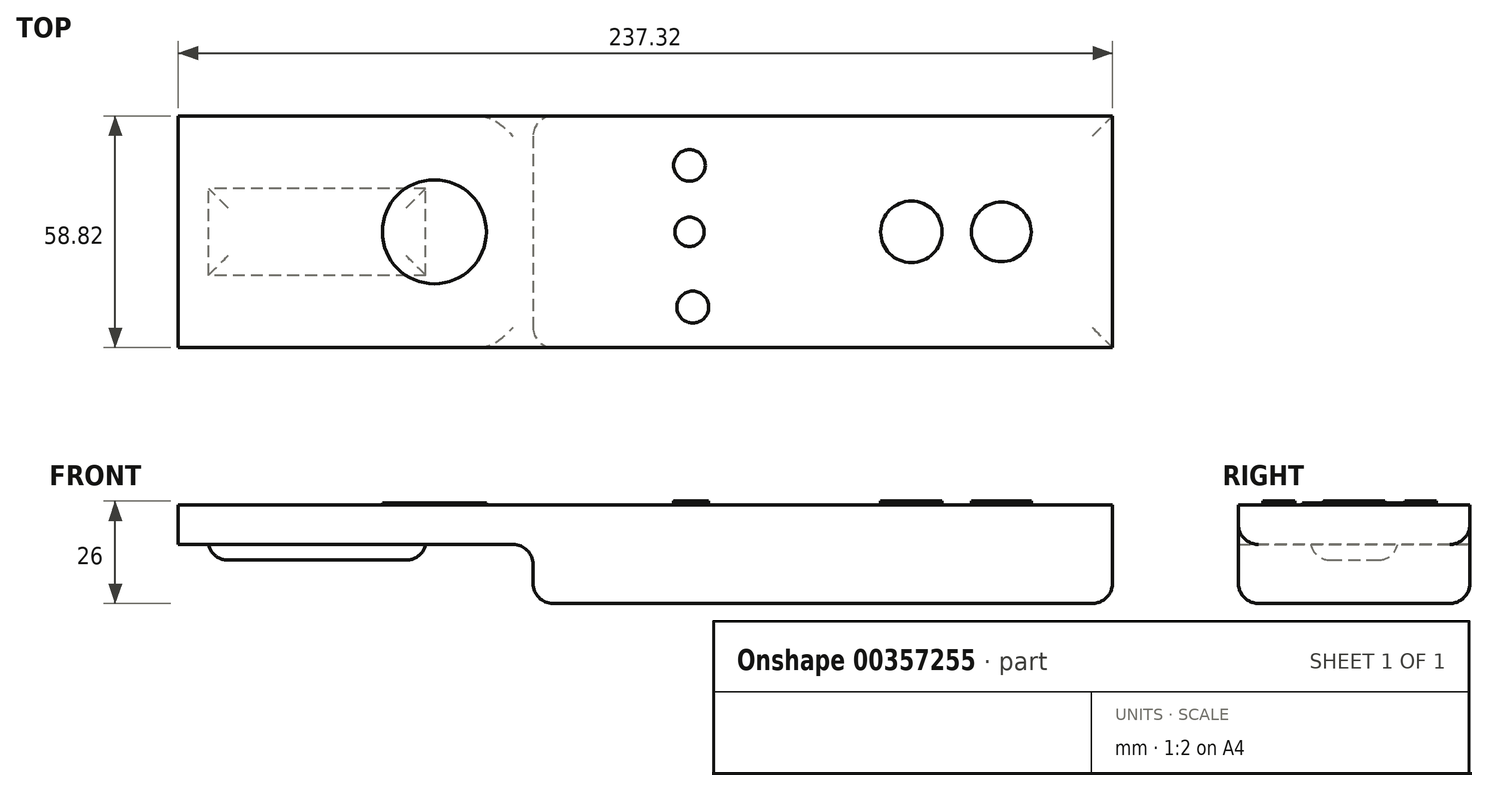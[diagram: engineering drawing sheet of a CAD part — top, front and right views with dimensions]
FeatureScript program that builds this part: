
annotation { "Feature Type Name" : "Feature", "Feature Type Description" : "" }
export const myFeature = defineFeature(function(context is Context, id is Id, definition is map)
    precondition{}
    {
        {
            var Q0;
            Q0=qCreatedBy(makeId("Top.planeOp"),FACE);
            var sketch = newSketch(context, id + "F0", { "sketchPlane" : qUnion([Q0])});
            skLineSegment(sketch, "E0.bottom", {"start": v(118.66, -29.4) * mm, "end": v(-118.66, -29.4) * mm});
            skLineSegment(sketch, "E0.top", {"start": v(118.66, 29.4) * mm, "end": v(-118.66, 29.4) * mm});
            skLineSegment(sketch, "E0.left", {"start": v(118.66, -29.4) * mm, "end": v(118.66, 29.4) * mm});
            skLineSegment(sketch, "E0.right", {"start": v(-118.66, -29.4) * mm, "end": v(-118.66, 29.4) * mm});
            skPoint(sketch, "E0.middle", {"position": v(0, 0) * mm});
            skSolve(sketch);
        }
        {
            var Q0;
            Q0 = qSketchRegion(id + "F0", true);
            extrude(context, id + "F1", {"entities" : qUnion([Q0]), "depth" : 10 * mm});
        }
        {
            var Q0;
            Q0=makeQuery(id+"F1.opExtrude","CAP_FACE",FACE,{"disambiguationData":[OSD([sQuery(id+"F0.wireOp",EDGE,"E0.bottom"),sQuery(id+"F0.wireOp",EDGE,"E0.top"),sQuery(id+"F0.wireOp",EDGE,"E0.left"),sQuery(id+"F0.wireOp",EDGE,"E0.right")])],"isStart":true});
            var sketch = newSketch(context, id + "F2", { "sketchPlane" : qUnion([Q0])});
            skLineSegment(sketch, "E1.bottom", {"start": v(118.66, -29.4) * mm, "end": v(-28.54, -29.4) * mm});
            skLineSegment(sketch, "E1.top", {"start": v(118.66, 29.4) * mm, "end": v(-28.54, 29.4) * mm});
            skLineSegment(sketch, "E1.left", {"start": v(118.66, -29.4) * mm, "end": v(118.66, 29.4) * mm});
            skLineSegment(sketch, "E1.right", {"start": v(-28.54, -29.4) * mm, "end": v(-28.54, 29.4) * mm});
            skPoint(sketch, "E1.middle", {"position": v(45.06, 0) * mm});
            skSolve(sketch);
        }
        {
            var Q0;
            Q0=makeQuery(id+"F2.imprint","IMPRINT",FACE,{"disambiguationData":[TD([[makeQuery(id+"F2.imprint","IMPRINT",EDGE,{"derivedFrom":sQuery(id+"F2.wireOp",EDGE,"E1.bottom")}),-1.0]])]});
            extrude(context, id + "F3", {"entities" : qUnion([Q0]), "operationType" : NewBodyOperationType.ADD, "depth" : 15 * mm});
        }
        {
            var Q0;
            Q0=makeQuery(id+"F3.opExtrude","SWEPT_FACE",FACE,{"disambiguationData":[OSD([sQuery(id+"F2.wireOp",EDGE,"E1.right")])]});
            var Q1;
            Q1=makeQuery(id+"F3.opExtrude","CAP_FACE",FACE,{"disambiguationData":[OSD([sQuery(id+"F2.wireOp",EDGE,"E1.bottom"),sQuery(id+"F2.wireOp",EDGE,"E1.top"),sQuery(id+"F2.wireOp",EDGE,"E1.left"),sQuery(id+"F2.wireOp",EDGE,"E1.right")])],"isStart":false});
            fillet(context, id + "F4", {"entities" : qUnion([Q0, Q1]), "radius" : 5.08 * mm, "tangentPropagation" : true, "allowEdgeOverflow" : false});
        }
        {
            var Q0;
            Q0=makeQuery(id+"F1.opExtrude","CAP_FACE",FACE,{"disambiguationData":[OSD([sQuery(id+"F0.wireOp",EDGE,"E0.bottom"),sQuery(id+"F0.wireOp",EDGE,"E0.top"),sQuery(id+"F0.wireOp",EDGE,"E0.left"),sQuery(id+"F0.wireOp",EDGE,"E0.right")])],"isStart":true});
            var sketch = newSketch(context, id + "F5", { "sketchPlane" : qUnion([Q0])});
            skLineSegment(sketch, "E2.bottom", {"start": v(-55.8, 11.04) * mm, "end": v(-111, 11.04) * mm});
            skLineSegment(sketch, "E2.top", {"start": v(-55.8, -11.04) * mm, "end": v(-111, -11.04) * mm});
            skLineSegment(sketch, "E2.left", {"start": v(-55.8, 11.04) * mm, "end": v(-55.8, -11.04) * mm});
            skLineSegment(sketch, "E2.right", {"start": v(-111, 11.04) * mm, "end": v(-111, -11.04) * mm});
            skPoint(sketch, "E2.middle", {"position": v(-83.4, 0) * mm});
            skSolve(sketch);
        }
        {
            var Q0;
            Q0 = qSketchRegion(id + "F5", true);
            extrude(context, id + "F6", {"entities" : qUnion([Q0]), "operationType" : NewBodyOperationType.ADD, "depth" : 4 * mm});
        }
        {
            var Q0;
            Q0=makeQuery(id+"F6.opExtrude","CAP_FACE",FACE,{"disambiguationData":[OSD([sQuery(id+"F5.wireOp",EDGE,"E2.bottom"),sQuery(id+"F5.wireOp",EDGE,"E2.top"),sQuery(id+"F5.wireOp",EDGE,"E2.left"),sQuery(id+"F5.wireOp",EDGE,"E2.right")])],"isStart":false});
            fillet(context, id + "F7", {"entities" : qUnion([Q0]), "radius" : 5.08 * mm, "tangentPropagation" : true, "allowEdgeOverflow" : false});
        }
        {
            var Q0;
            Q0=makeQuery(id+"F1.opExtrude","CAP_FACE",FACE,{"disambiguationData":[OSD([sQuery(id+"F0.wireOp",EDGE,"E0.bottom"),sQuery(id+"F0.wireOp",EDGE,"E0.top"),sQuery(id+"F0.wireOp",EDGE,"E0.left"),sQuery(id+"F0.wireOp",EDGE,"E0.right")])],"isStart":false});
            var sketch = newSketch(context, id + "F8", { "sketchPlane" : qUnion([Q0])});
            skSolve(sketch);
        }
        {
            var Q0;
            Q0=makeQuery(id+"F8.imprint","IMPRINT",FACE,{"disambiguationData":[TD([[makeQuery(id+"F8.imprint","IMPRINT",EDGE,{"derivedFrom":makeQuery(id+"F1.opExtrude","CAP_EDGE",EDGE,{"disambiguationData":[OSD([sQuery(id+"F0.wireOp",EDGE,"E0.bottom")])],"isStart":false})}),-1.0]])]});
            var sketch = newSketch(context, id + "F9", { "sketchPlane" : qUnion([Q0])});
            skCircle(sketch, "E3", {"center": v(-53.6, 0) * mm, "radius": 13.21 * mm});
            skSolve(sketch);
        }
        {
            var Q0;
            Q0=makeQuery(id+"F9.imprint","IMPRINT",FACE,{"disambiguationData":[TD([[makeQuery(id+"F9.imprint","IMPRINT",EDGE,{"derivedFrom":sQuery(id+"F9.wireOp",EDGE,"E3")}),1.0]])]});
            extrude(context, id + "F10", {"entities" : qUnion([Q0]), "operationType" : NewBodyOperationType.ADD, "depth" : 0.5 * mm});
        }
        {
            var Q0;
            Q0=makeQuery(id+"F10.opExtrude","CAP_FACE",FACE,{"disambiguationData":[OSD([sQuery(id+"F9.wireOp",EDGE,"E3")])],"isStart":false});
            var sketch = newSketch(context, id + "F11", { "sketchPlane" : qUnion([Q0])});
            skCircle(sketch, "E4", {"center": v(12.05, -19.12) * mm, "radius": 4.05 * mm});
            skCircle(sketch, "E5", {"center": v(11.2, 0) * mm, "radius": 3.73 * mm});
            skCircle(sketch, "E6", {"center": v(11.2, 16.88) * mm, "radius": 4.02 * mm});
            skCircle(sketch, "E7", {"center": v(67.58, 0) * mm, "radius": 7.8 * mm});
            skCircle(sketch, "E8", {"center": v(90.44, 0) * mm, "radius": 7.58 * mm});
            skSolve(sketch);
        }
        {
            var Q0;
            Q0 = qSketchRegion(id + "F11", true);
            extrude(context, id + "F12", {"entities" : qUnion([Q0]), "depth" : 0.5 * mm});
        }
    });
